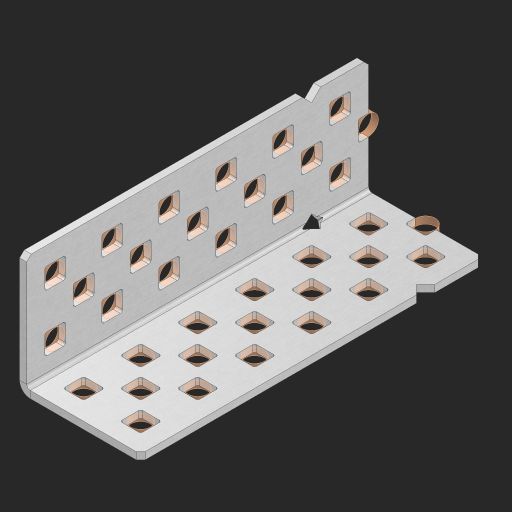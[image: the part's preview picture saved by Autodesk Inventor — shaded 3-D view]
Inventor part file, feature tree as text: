
AUTODESK INVENTOR PART (.ipt)
format: ipt  version: 2023 (Build 270158000, 158)  size: 813,056 bytes
history: native  units: in
note: dims shown in document units (in); Inventor stores cm internally (conversion verified against a paired STEP export)
features: other x42, extrude x34, sheet_metal_op x8, sketch x7, pattern_linear x2, mirror x1, chamfer x1
ambient origin geometry x8: Origin, YZ Plane, XZ Plane, XY Plane, X Axis, Y Axis, Z Axis, Center Point
bodies: Solid1 (feature_tree), Body (feature_tree)
feature tree (95):
  sheet_metal_op  "Flanges"
  sheet_metal_op  "Body Pattern"
  pattern_linear  "Center Pattern"  Spacing1=1.0in  [1 undecoded]
  other  "Arc Length"
  pattern_linear  "Notch Pattern"  Spacing1=0.25in  [1 undecoded]
  other  "Diagonal Plane"
  mirror  "Everything Mirrored"
  chamfer  "End Chamfer"
  sketch  "Sketch1"  dims[d0=1.0in]
  other  "Plate1"
  sketch  "Sketch2"  dims[d1=3.0in]
  other  "Plate2"
  sheet_metal_op  "Bend1"
  sheet_metal_op  "Corner1"
  sketch  "Sketch8"  dims[d2=0.0625in]
  sketch  "Sketch9"  dims[d3=0.0625in]
  other  "Srf91"
  sheet_metal_op  "Body Pattern Sketch"
  other  "Srf92"
  sketch  "Sketch13"  dims[d4=0.0312in]
  sketch  "Sketch15"  dims[d5=0.125in]
  sketch  "Sketch16"  dims[d6=0.0625in d7=1.0in d8=90.0deg d9=0.0312in d10=0.25in d11=0.0625in d12=0.0625in d49=0.182in d50=0.02in d52=0.25in d53=0.0625in d54=0.0in d55=0.172in d56=1.0in d57=0.0in d60=2.3622in d62=0.5in d63=0.7874in d65=0.5in d85=0.1473in d86=0.1782in d89=0.0625in d90=0.0in d91=0.04in d92=0.0491in d95=2.5in d96=0.04in d97=0.25in d98=45.0deg d99=0.25in d106=0.182in d107=0.02in d108=0.5in d110=0.0625in d111=0.0in d112=0.172in d113=0.5in d114=0.0in d117=0.5in d123=0.25in d125=0.25in d126=0.0491in d127=0.1473in d128=0.08in d129=0.04in d130=2.5in]
  other  "Srf786"
  other  "Srf856"
  other  "Srf857"
  other  "Srf858"
  other  "Srf859"
  other  "Srf860"
  other  "Srf861"
  other  "Srf889"
  other  "Srf890"
  other  "Srf891"
  other  "Srf1275"
  other  "Srf1276"
  other  "Srf1278"
  other  "Srf1279"
  other  "Srf1280"
  other  "Srf1281"
  other  "Srf1282"
  other  "Srf1283"
  other  "Srf1277"
  other  "Srf1285"
  other  "Srf1286"
  other  "Srf1287"
  other  "Srf1383"
  other  "Srf1384"
  other  "Srf1385"
  other  "Srf1386"
  other  "Srf1445"
  other  "Srf1446"
  other  "Srf1475"
  other  "Srf1476"
  other  "Srf1477"
  other  "Srf1478"
  other  "Srf1537"
  other  "Srf1538"
  sheet_metal_op  "Body Stamp"
  sheet_metal_op  "Body Circle"
  other  "Center Stamp"
  other  "Center Circle"
  sheet_metal_op  "Notch"
  extrude  "ExtrusionSrf92"  Depth=0.0625in
  extrude  "ExtrusionSrf856"  Depth=0.0625in
  extrude  "ExtrusionSrf857"  Depth=0.182in
  extrude  "ExtrusionSrf858"  Depth=0.02in
  extrude  "ExtrusionSrf859"  Depth=0.25in
  extrude  "ExtrusionSrf860"  Depth=0.0625in
  extrude  "ExtrusionSrf861"  TaperAngle=0.0deg  [1 undecoded]
  extrude  "ExtrusionSrf889"  Depth=2.5in
  extrude  "ExtrusionSrf890"  Depth=1.0in TaperAngle=0.0deg
  extrude  "ExtrusionSrf891"  Depth=2.5in
  extrude  "ExtrusionSrf1275"  Depth=0.5in
  extrude  "ExtrusionSrf1276"  Depth=2.5in
  extrude  "ExtrusionSrf1277"  Depth=2.5in
  extrude  "ExtrusionSrf1278"  Depth=0.0625in
  extrude  "ExtrusionSrf1279"  Depth=2.5in TaperAngle=0.0deg
  extrude  "ExtrusionSrf1280"  Depth=2.5in
  extrude  "ExtrusionSrf1281"  Depth=0.25in TaperAngle=45.0deg
  extrude  "ExtrusionSrf1282"  Depth=0.25in
  extrude  "ExtrusionSrf1345"  Depth=0.182in
  extrude  "ExtrusionSrf1346"  Depth=0.02in
  extrude  "ExtrusionSrf1347"  Depth=0.5in
  extrude  "ExtrusionSrf1348"  Depth=0.0625in
  extrude  "ExtrusionSrf1383"  TaperAngle=0.0deg  [1 undecoded]
  extrude  "ExtrusionSrf1384"  Depth=2.5in
  extrude  "ExtrusionSrf1385"  Depth=0.5in TaperAngle=0.0deg
  extrude  "ExtrusionSrf1386"  Depth=0.5in
  extrude  "ExtrusionSrf1445"  Depth=0.25in
  extrude  "ExtrusionSrf1446"  Depth=0.25in
  extrude  "ExtrusionSrf1475"  Depth=2.5in
  extrude  "ExtrusionSrf1476"  Depth=2.5in
  extrude  "ExtrusionSrf1477"  Depth=2.5in
  extrude  "ExtrusionSrf1478"  Depth=2.5in
  extrude  "ExtrusionSrf1537"  Depth=2.5in
  extrude  "ExtrusionSrf1538"  [1 undecoded]
note: 5 required parameter values undecoded (feature->parameter linkage not recoverable at this tier; creation-order binding heuristic only, values carry confidence <= 0.55)
